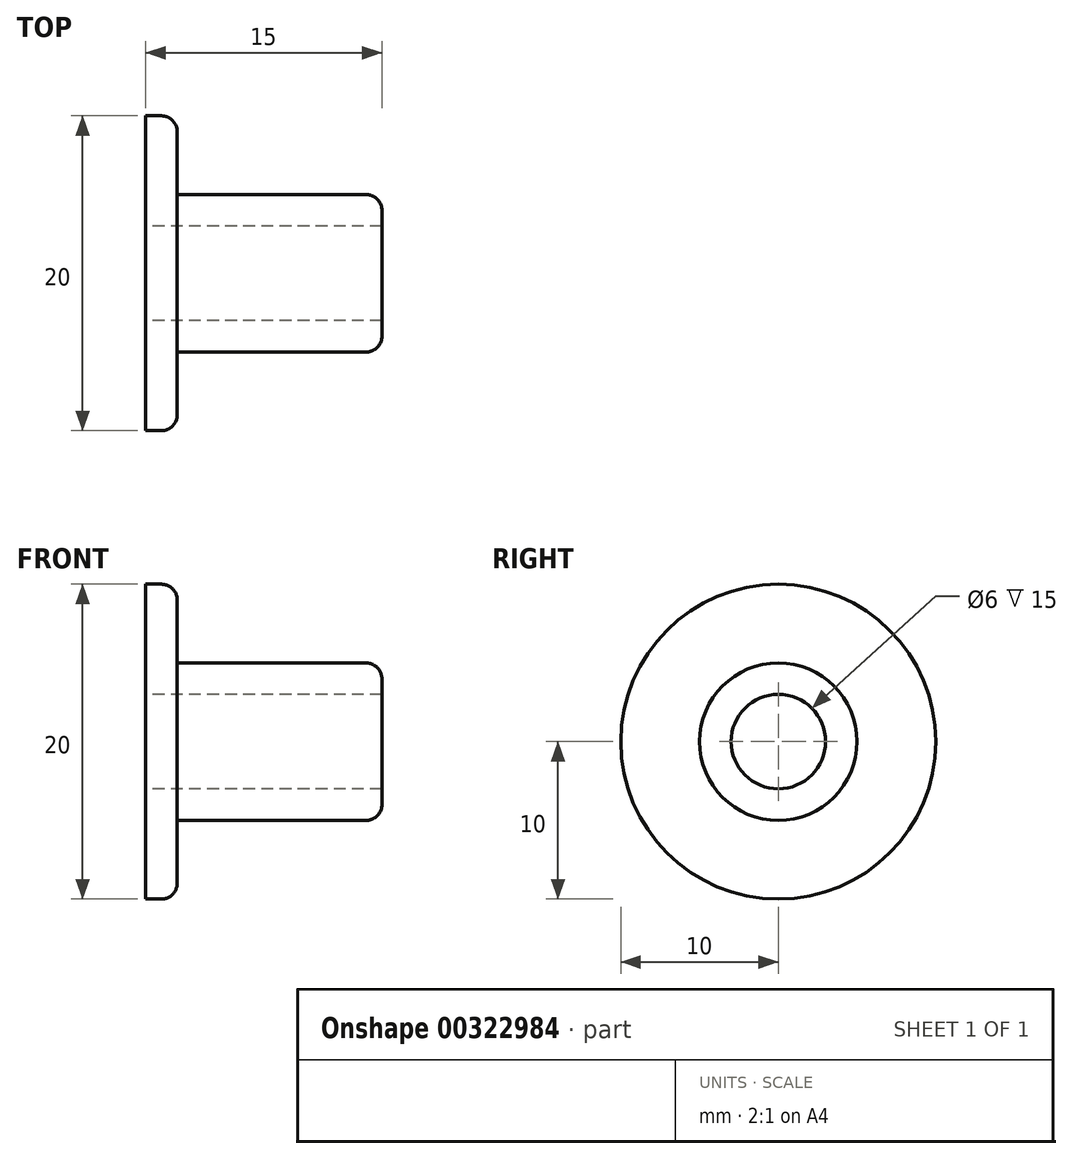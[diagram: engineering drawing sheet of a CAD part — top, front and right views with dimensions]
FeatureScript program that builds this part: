
annotation { "Feature Type Name" : "Feature", "Feature Type Description" : "" }
export const myFeature = defineFeature(function(context is Context, id is Id, definition is map)
    precondition{}
    {
        {
            var Q0;
            Q0=qCreatedBy(makeId("Front.planeOp"),FACE);
            var sketch = newSketch(context, id + "F0", { "sketchPlane" : qUnion([Q0])});
            skLineSegment(sketch, "E0", {"start": v(0, 0) * mm, "end": v(0, 3) * mm, "construction": true});
            skLineSegment(sketch, "E1", {"start": v(0, 3) * mm, "end": v(15, 3) * mm});
            skLineSegment(sketch, "E2", {"start": v(0, 3) * mm, "end": v(0, 10) * mm});
            skLineSegment(sketch, "E3", {"start": v(0, 10) * mm, "end": v(2, 10) * mm});
            skLineSegment(sketch, "E4", {"start": v(15, 3) * mm, "end": v(15, 5) * mm});
            skLineSegment(sketch, "E5", {"start": v(15, 5) * mm, "end": v(0, 5) * mm, "construction": true});
            skLineSegment(sketch, "E6", {"start": v(2, 10) * mm, "end": v(2, 5) * mm});
            skLineSegment(sketch, "E7", {"start": v(15, 5) * mm, "end": v(2, 5) * mm});
            skLineSegment(sketch, "E8", {"start": v(0.49, 0) * mm, "end": v(2, 0) * mm});
            skLineSegment(sketch, "E9", {"start": v(2, 0) * mm, "end": v(16.87, 0) * mm, "construction": true});
            skSolve(sketch);
        }
        {
            var Q0;
            Q0=makeQuery(id+"F0.imprint","IMPRINT",FACE,{"disambiguationData":[TD([[makeQuery(id+"F0.imprint","IMPRINT",EDGE,{"derivedFrom":sQuery(id+"F0.wireOp",EDGE,"E1")}),1.0]])]});
            var Q1;
            Q1=sQuery(id+"F0.wireOp",EDGE,"E9");
            revolve(context, id + "F1", {"entities" : qUnion([Q0]), "axis" : qUnion([Q1]), "revolveType" : RevolveType.FULL});
        }
        {
            var Q0;
            Q0=makeQuery(id+"F1.opRevolve","SWEPT_EDGE",EDGE,{"disambiguationData":[OSD([sQuery(id+"F0.wireOp",EDGE,"E4"),sQuery(id+"F0.wireOp",EDGE,"E7")])]});
            var Q1;
            Q1=makeQuery(id+"F1.opRevolve","SWEPT_EDGE",EDGE,{"disambiguationData":[OSD([sQuery(id+"F0.wireOp",EDGE,"E3"),sQuery(id+"F0.wireOp",EDGE,"E6")])]});
            fillet(context, id + "F2", {"entities" : qUnion([Q0, Q1]), "radius" : 1 * mm, "tangentPropagation" : true, "allowEdgeOverflow" : false});
        }
    });
